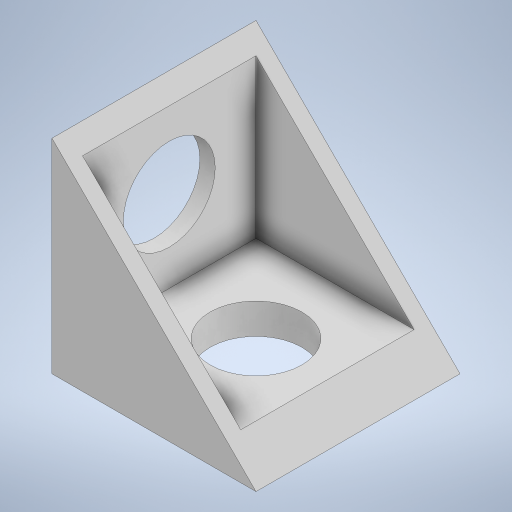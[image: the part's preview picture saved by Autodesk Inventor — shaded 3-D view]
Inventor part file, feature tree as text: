
AUTODESK INVENTOR PART (.ipt)
format: ipt  version: 2023.1 (Build 271208000, 208)  size: 244,736 bytes
history: native  units: in
note: dims shown in document units (in); Inventor stores cm internally (conversion verified against a paired STEP export)
features: extrude x5, sketch x5
ambient origin geometry x8: Origin, YZ Plane, XZ Plane, XY Plane, X Axis, Y Axis, Z Axis, Center Point
bodies: Solid1 (feature_tree)
feature tree (10):
  extrude  "Extrusion1"  Depth=0.7874in
  extrude  "Extrusion2"  Depth=0.6693in
  extrude  "Extrusion6"  Depth=0.6693in TaperAngle=0.0deg
  sketch  "Sketch7"  dims[d16=0.0in d17=0.0in d18=0.315in]
  extrude  "Extrusion7"  Depth=0.315in
  extrude  "Extrusion8"  Depth=0.3937in
  sketch  "Sketch1"  dims[d0=0.7874in d1=0.7874in]
  sketch  "Sketch2"  dims[d2=0.7874in d3=0.0in d4=0.6693in]
  sketch  "Sketch6"  dims[d5=0.6693in d6=0.6693in d7=0.0in]
  sketch  "Sketch8"  dims[d19=0.3543in d20=0.3543in d21=0.3937in d22=0.0in d23=0.3937in d24=0.0in]
